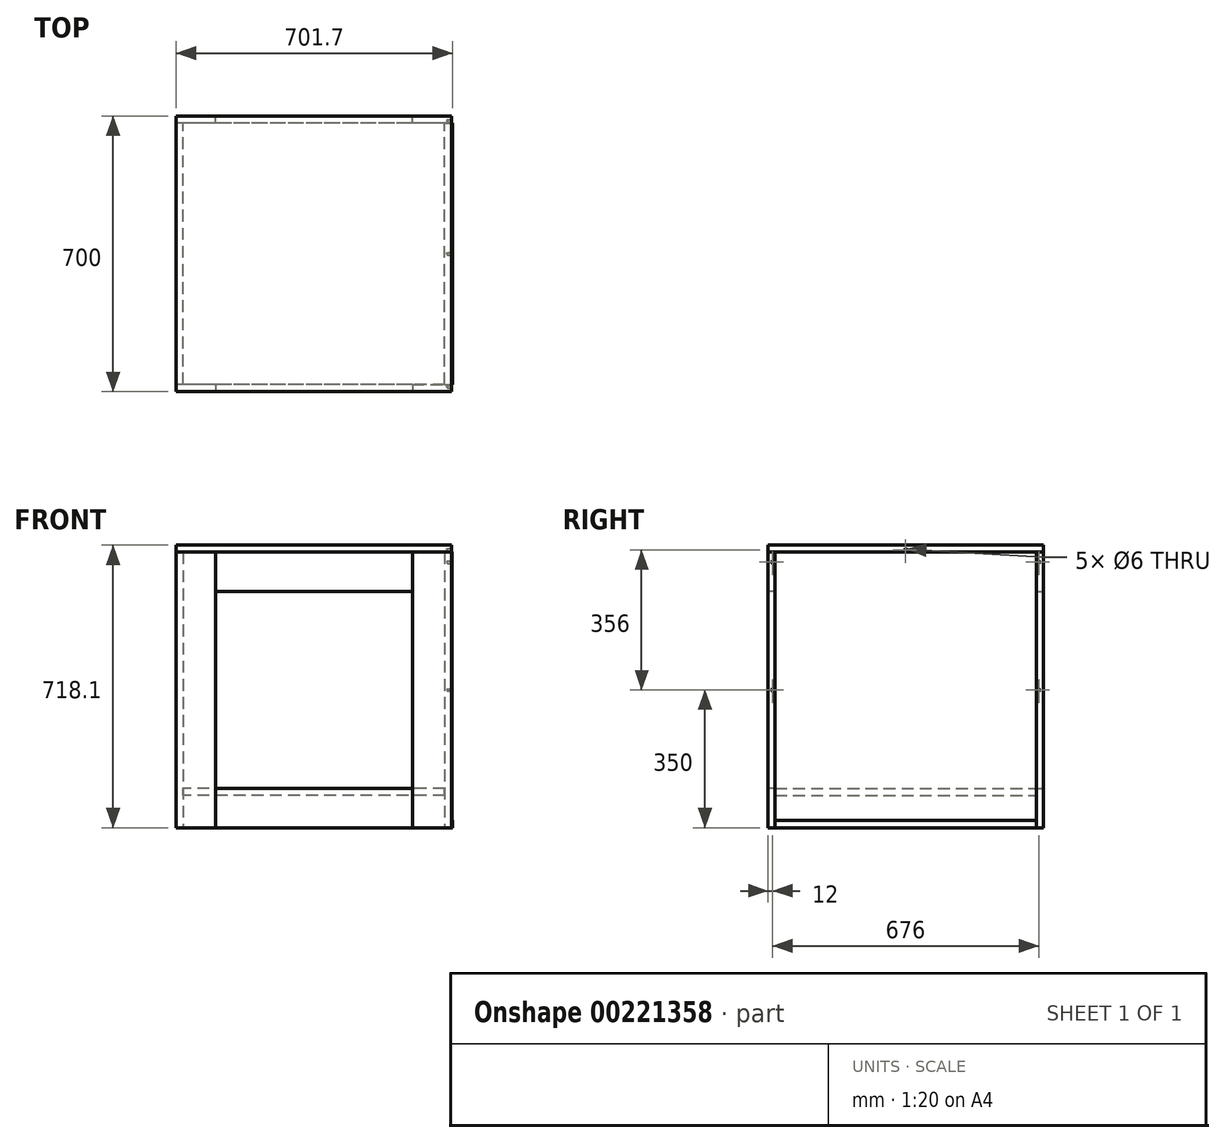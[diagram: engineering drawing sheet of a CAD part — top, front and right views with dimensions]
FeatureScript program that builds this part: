
annotation { "Feature Type Name" : "Feature", "Feature Type Description" : "" }
export const myFeature = defineFeature(function(context is Context, id is Id, definition is map)
    precondition{}
    {
        {
            var Q0;
            Q0=qCreatedBy(makeId("Top.planeOp"),FACE);
            var sketch = newSketch(context, id + "F0", { "sketchPlane" : qUnion([Q0])});
            skLineSegment(sketch, "E0.bottom", {"start": v(350, -350) * mm, "end": v(-350, -350) * mm});
            skLineSegment(sketch, "E0.top", {"start": v(350, 350) * mm, "end": v(-350, 350) * mm});
            skLineSegment(sketch, "E0.left", {"start": v(350, -350) * mm, "end": v(350, 350) * mm});
            skLineSegment(sketch, "E0.right", {"start": v(-350, -350) * mm, "end": v(-350, 350) * mm});
            skPoint(sketch, "E0.middle", {"position": v(0, 0) * mm});
            skLineSegment(sketch, "E1.0", {"start": v(332, 332) * mm, "end": v(-332, 332) * mm});
            skLineSegment(sketch, "E1.1", {"start": v(332, -332) * mm, "end": v(332, 332) * mm});
            skLineSegment(sketch, "E1.2", {"start": v(332, -332) * mm, "end": v(-332, -332) * mm});
            skLineSegment(sketch, "E1.3", {"start": v(-332, -332) * mm, "end": v(-332, 332) * mm});
            skLineSegment(sketch, "E2", {"start": v(-332, 332) * mm, "end": v(-350, 332) * mm});
            skLineSegment(sketch, "E3", {"start": v(-332, -332) * mm, "end": v(-350, -332) * mm});
            skLineSegment(sketch, "E4", {"start": v(-250, -332) * mm, "end": v(-250, -350) * mm});
            skLineSegment(sketch, "E5.MirrorCS", {"start": v(-250, 332) * mm, "end": v(-250, 350) * mm});
            skLineSegment(sketch, "E6.MirrorCS", {"start": v(250, 332) * mm, "end": v(250, 350) * mm});
            skLineSegment(sketch, "E7.MirrorCS", {"start": v(332, 332) * mm, "end": v(350, 332) * mm});
            skLineSegment(sketch, "E8.MirrorCS", {"start": v(332, -332) * mm, "end": v(350, -332) * mm});
            skLineSegment(sketch, "E9.MirrorCS", {"start": v(250, -332) * mm, "end": v(250, -350) * mm});
            skSolve(sketch);
        }
        {
            var Q0;
            {var subQ0=sQuery(id+"F0.wireOp",EDGE,"E3");Q0=makeQuery(id+"F0.imprint","IMPRINT",FACE,{"disambiguationData":[TD([[makeQuery(id+"F0.imprint","IMPRINT",EDGE,{"derivedFrom":subQ0}),1.0]])]});}
            var Q1;
            {var subQ0=sQuery(id+"F0.wireOp",EDGE,"E8.MirrorCS");Q1=makeQuery(id+"F0.imprint","IMPRINT",FACE,{"disambiguationData":[TD([[makeQuery(id+"F0.imprint","IMPRINT",EDGE,{"derivedFrom":subQ0}),-1.0]])]});}
            var Q2;
            {var subQ4=sQuery(id+"F0.wireOp",EDGE,"E6.MirrorCS");Q2=makeQuery(id+"F0.imprint","IMPRINT",FACE,{"disambiguationData":[TD([[makeQuery(id+"F0.imprint","IMPRINT",EDGE,{"derivedFrom":subQ4}),-1.0]])]});}
            var Q3;
            {var subQ0=sQuery(id+"F0.wireOp",EDGE,"E2");Q3=makeQuery(id+"F0.imprint","IMPRINT",FACE,{"disambiguationData":[TD([[makeQuery(id+"F0.imprint","IMPRINT",EDGE,{"derivedFrom":subQ0}),-1.0]])]});}
            extrude(context, id + "F1", {"entities" : qUnion([Q0, Q1, Q2, Q3]), "depth" : 700 * mm, "offsetDistance" : 25 * mm});
        }
        {
            var Q0;
            Q0=makeQuery(id+"F0.imprint","IMPRINT",FACE,{"disambiguationData":[TD([[makeQuery(id+"F0.imprint","IMPRINT",EDGE,{"derivedFrom":sQuery(id+"F0.wireOp",EDGE,"E1.3")}),1.0]])]});
            var Q1;
            Q1=makeQuery(id+"F0.imprint","IMPRINT",FACE,{"disambiguationData":[TD([[makeQuery(id+"F0.imprint","IMPRINT",EDGE,{"derivedFrom":sQuery(id+"F0.wireOp",EDGE,"E1.1")}),-1.0]])]});
            var Q2;
            Q2=makeQuery(id+"F1.opExtrude","CAP_FACE",FACE,{"disambiguationData":[OSD([sQuery(id+"F0.wireOp",EDGE,"E0.top"),sQuery(id+"F0.wireOp",EDGE,"E0.right"),sQuery(id+"F0.wireOp",EDGE,"E1.0"),sQuery(id+"F0.wireOp",EDGE,"E2"),sQuery(id+"F0.wireOp",EDGE,"E5.MirrorCS")])],"isStart":false});
            extrude(context, id + "F2", {"entities" : qUnion([Q0, Q1]), "endBound" : BoundingType.UP_TO_SURFACE, "depth" : 25 * mm, "endBoundEntityFace" : qUnion([Q2]), "offsetDistance" : 25 * mm});
        }
        {
            var Q0;
            {var subQ2=sQuery(id+"F0.wireOp",EDGE,"E4");Q0=makeQuery(id+"F0.imprint","IMPRINT",FACE,{"disambiguationData":[TD([[makeQuery(id+"F0.imprint","IMPRINT",EDGE,{"derivedFrom":subQ2}),1.0]])]});}
            var Q1;
            {var subQ2=sQuery(id+"F0.wireOp",EDGE,"E5.MirrorCS");Q1=makeQuery(id+"F0.imprint","IMPRINT",FACE,{"disambiguationData":[TD([[makeQuery(id+"F0.imprint","IMPRINT",EDGE,{"derivedFrom":subQ2}),-1.0]])]});}
            extrude(context, id + "F3", {"entities" : qUnion([Q0, Q1]), "depth" : 100 * mm, "offsetDistance" : 25 * mm});
        }
        {
            var Q0;
            Q0=makeQuery(id+"F1.opExtrude","CAP_FACE",FACE,{"disambiguationData":[OSD([sQuery(id+"F0.wireOp",EDGE,"E0.bottom"),sQuery(id+"F0.wireOp",EDGE,"E0.right"),sQuery(id+"F0.wireOp",EDGE,"E1.2"),sQuery(id+"F0.wireOp",EDGE,"E3"),sQuery(id+"F0.wireOp",EDGE,"E4")])],"isStart":false});
            var sketch = newSketch(context, id + "F4", { "sketchPlane" : qUnion([Q0])});
            skLineSegment(sketch, "E10.0", {"start": v(-250, -332) * mm, "end": v(-250, -350) * mm});
            skLineSegment(sketch, "E10.1", {"start": v(250, -332) * mm, "end": v(-250, -332) * mm});
            skLineSegment(sketch, "E10.2", {"start": v(250, -350) * mm, "end": v(-250, -350) * mm});
            skLineSegment(sketch, "E10.3", {"start": v(250, -332) * mm, "end": v(250, -350) * mm});
            skLineSegment(sketch, "E10.4", {"start": v(250, 332) * mm, "end": v(-250, 332) * mm});
            skLineSegment(sketch, "E10.5", {"start": v(250, 350) * mm, "end": v(-250, 350) * mm});
            skLineSegment(sketch, "E10.6", {"start": v(-250, 332) * mm, "end": v(-250, 350) * mm});
            skLineSegment(sketch, "E10.7", {"start": v(250, 332) * mm, "end": v(250, 350) * mm});
            skSolve(sketch);
        }
        {
            var Q0;
            Q0=makeQuery(id+"F4.imprint","IMPRINT",FACE,{"disambiguationData":[TD([[makeQuery(id+"F4.imprint","IMPRINT",EDGE,{"derivedFrom":sQuery(id+"F4.wireOp",EDGE,"E10.4")}),-1.0]])]});
            var Q1;
            Q1=makeQuery(id+"F4.imprint","IMPRINT",FACE,{"disambiguationData":[TD([[makeQuery(id+"F4.imprint","IMPRINT",EDGE,{"derivedFrom":sQuery(id+"F4.wireOp",EDGE,"E10.0")}),1.0]])]});
            extrude(context, id + "F5", {"entities" : qUnion([Q0, Q1]), "oppositeDirection" : true, "depth" : 100 * mm, "offsetDistance" : 25 * mm});
        }
        {
            var Q0;
            Q0=makeQuery(id+"F3.opExtrude","CAP_FACE",FACE,{"disambiguationData":[OSD([sQuery(id+"F0.wireOp",EDGE,"E0.top"),sQuery(id+"F0.wireOp",EDGE,"E1.0"),sQuery(id+"F0.wireOp",EDGE,"E5.MirrorCS"),sQuery(id+"F0.wireOp",EDGE,"E6.MirrorCS")])],"isStart":false});
            var sketch = newSketch(context, id + "F6", { "sketchPlane" : qUnion([Q0])});
            skLineSegment(sketch, "E11.0", {"start": v(332, 332) * mm, "end": v(-332, 332) * mm});
            skLineSegment(sketch, "E11.1", {"start": v(-332, -332) * mm, "end": v(-332, 332) * mm});
            skLineSegment(sketch, "E11.2", {"start": v(332, -332) * mm, "end": v(-332, -332) * mm});
            skLineSegment(sketch, "E11.3", {"start": v(332, -332) * mm, "end": v(332, 332) * mm});
            skSolve(sketch);
        }
        {
            var Q0;
            {var subQ0=sQuery(id+"F6.wireOp",EDGE,"E11.1");Q0=makeQuery(id+"F6.imprint","IMPRINT",FACE,{"disambiguationData":[TD([[makeQuery(id+"F6.imprint","IMPRINT",EDGE,{"derivedFrom":subQ0}),-1.0]])]});}
            extrude(context, id + "F7", {"entities" : qUnion([Q0]), "oppositeDirection" : true, "depth" : 18 * mm, "offsetDistance" : 25 * mm});
        }
        {
            var Q0;
            Q0=makeQuery(id+"F2.opExtrude","CAP_FACE",FACE,{"disambiguationData":[OSD([sQuery(id+"F0.wireOp",EDGE,"E0.right"),sQuery(id+"F0.wireOp",EDGE,"E1.3"),sQuery(id+"F0.wireOp",EDGE,"E2"),sQuery(id+"F0.wireOp",EDGE,"E3")])],"isStart":false});
            var sketch = newSketch(context, id + "F8", { "sketchPlane" : qUnion([Q0])});
            skLineSegment(sketch, "E12.0", {"start": v(-250, 350) * mm, "end": v(-350, 350) * mm});
            skLineSegment(sketch, "E12.1", {"start": v(250, 350) * mm, "end": v(-250, 350) * mm});
            skLineSegment(sketch, "E12.2", {"start": v(-350, -332) * mm, "end": v(-350, 332) * mm});
            skLineSegment(sketch, "E12.3", {"start": v(-350, 332) * mm, "end": v(-350, 350) * mm});
            skLineSegment(sketch, "E12.4", {"start": v(-250, -350) * mm, "end": v(-350, -350) * mm});
            skLineSegment(sketch, "E12.5", {"start": v(-350, -350) * mm, "end": v(-350, -332) * mm});
            skLineSegment(sketch, "E12.6", {"start": v(250, -350) * mm, "end": v(-250, -350) * mm});
            skLineSegment(sketch, "E12.7", {"start": v(350, -350) * mm, "end": v(250, -350) * mm});
            skLineSegment(sketch, "E12.8", {"start": v(350, -350) * mm, "end": v(350, -332) * mm});
            skLineSegment(sketch, "E12.9", {"start": v(350, -332) * mm, "end": v(350, 332) * mm});
            skLineSegment(sketch, "E12.10", {"start": v(350, 332) * mm, "end": v(350, 350) * mm});
            skLineSegment(sketch, "E12.11", {"start": v(350, 350) * mm, "end": v(250, 350) * mm});
            skSolve(sketch);
        }
        {
            var Q0;
            Q0=makeQuery(id+"F8.imprint","IMPRINT",FACE,{"disambiguationData":[TD([[makeQuery(id+"F8.imprint","IMPRINT",EDGE,{"derivedFrom":sQuery(id+"F8.wireOp",EDGE,"E12.0")}),1.0]])]});
            var Q1;
            Q1=makeQuery(id+"F8.imprint","IMPRINT",FACE,{"disambiguationData":[TD([[makeQuery(id+"F8.imprint","IMPRINT",EDGE,{"derivedFrom":sQuery(id+"F8.wireOp",EDGE,"E12.2")}),-1.0]])]});
            extrude(context, id + "F9", {"entities" : qUnion([Q0, Q1]), "depth" : 18 * mm, "offsetDistance" : 25 * mm});
        }
        {
            var Q0;
            Q0=makeQuery(id+"F9.opExtrude","CAP_FACE",FACE,{"disambiguationData":[OSD([sQuery(id+"F8.wireOp",EDGE,"E12.0"),sQuery(id+"F8.wireOp",EDGE,"E12.1"),sQuery(id+"F8.wireOp",EDGE,"E12.2"),sQuery(id+"F8.wireOp",EDGE,"E12.3"),sQuery(id+"F8.wireOp",EDGE,"E12.4"),sQuery(id+"F8.wireOp",EDGE,"E12.5"),sQuery(id+"F8.wireOp",EDGE,"E12.6"),sQuery(id+"F8.wireOp",EDGE,"E12.7"),sQuery(id+"F8.wireOp",EDGE,"E12.8"),sQuery(id+"F8.wireOp",EDGE,"E12.9"),sQuery(id+"F8.wireOp",EDGE,"E12.10"),sQuery(id+"F8.wireOp",EDGE,"E12.11")])],"isStart":false});
            extrude(context, id + "F10", {"entities" : qUnion([Q0]), "depth" : 0.1 * mm, "offsetDistance" : 25 * mm});
        }
        {
            var Q0;
            Q0=makeQuery(id+"F2.opExtrude","SWEPT_FACE",FACE,{"disambiguationData":[OSD([sQuery(id+"F0.wireOp",EDGE,"E0.right")])]});
            extrude(context, id + "F11", {"entities" : qUnion([Q0]), "depth" : 0.1 * mm, "offsetDistance" : 25 * mm});
        }
        {
            var Q0;
            Q0=makeQuery(id+"F2.opExtrude","SWEPT_FACE",FACE,{"disambiguationData":[OSD([sQuery(id+"F0.wireOp",EDGE,"E0.left")])]});
            var sketch = newSketch(context, id + "F12", { "sketchPlane" : qUnion([Q0])});
            skLineSegment(sketch, "E13.0", {"start": v(-332, 700) * mm, "end": v(332, 700) * mm});
            skLineSegment(sketch, "E13.1", {"start": v(-332, 700) * mm, "end": v(-332, 0) * mm});
            skLineSegment(sketch, "E13.2", {"start": v(332, 700) * mm, "end": v(332, 0) * mm});
            skLineSegment(sketch, "E13.3", {"start": v(-332, 0) * mm, "end": v(332, 0) * mm});
            skLineSegment(sketch, "E14", {"start": v(-332, 18) * mm, "end": v(332, 18) * mm});
            skSolve(sketch);
        }
        {
            var Q0;
            {var subQ0=sQuery(id+"F12.wireOp",EDGE,"E13.0");Q0=makeQuery(id+"F12.imprint","IMPRINT",FACE,{"disambiguationData":[TD([[makeQuery(id+"F12.imprint","IMPRINT",EDGE,{"derivedFrom":subQ0}),-1.0]])]});}
            extrude(context, id + "F13", {"entities" : qUnion([Q0]), "depth" : 0.1 * mm, "offsetDistance" : 25 * mm});
        }
        {
            var Q0;
            Q0=makeQuery(id+"F13.opExtrude","CAP_FACE",FACE,{"disambiguationData":[OSD([sQuery(id+"F12.wireOp",EDGE,"E13.0"),sQuery(id+"F12.wireOp",EDGE,"E13.1"),sQuery(id+"F12.wireOp",EDGE,"E13.2"),sQuery(id+"F12.wireOp",EDGE,"E14")])],"isStart":false});
            var sketch = newSketch(context, id + "F14", { "sketchPlane" : qUnion([Q0])});
            skLineSegment(sketch, "E15.0", {"start": v(-332, 700) * mm, "end": v(-332, 0) * mm});
            skLineSegment(sketch, "E15.1", {"start": v(-332, 0) * mm, "end": v(332, 0) * mm});
            skLineSegment(sketch, "E15.2", {"start": v(332, 700) * mm, "end": v(332, 0) * mm});
            skLineSegment(sketch, "E15.3", {"start": v(-332, 700) * mm, "end": v(332, 700) * mm});
            skSolve(sketch);
        }
        {
            var Q0;
            {var subQ2=sQuery(id+"F14.wireOp",EDGE,"E15.1");Q0=makeQuery(id+"F14.imprint","IMPRINT",FACE,{"disambiguationData":[TD([[makeQuery(id+"F14.imprint","IMPRINT",EDGE,{"derivedFrom":subQ2}),1.0]])]});}
            var Q1;
            {var subQ0=sQuery(id+"F14.wireOp",EDGE,"E15.3");Q1=makeQuery(id+"F14.imprint","IMPRINT",FACE,{"disambiguationData":[TD([[makeQuery(id+"F14.imprint","IMPRINT",EDGE,{"derivedFrom":subQ0}),-1.0]])]});}
            extrude(context, id + "F15", {"entities" : qUnion([Q0, Q1]), "depth" : 1 * mm, "offsetDistance" : 25 * mm});
        }
        {
            var Q0;
            Q0=makeQuery(id+"F15.opExtrude","CAP_FACE",FACE,{"disambiguationData":[OSD([sQuery(id+"F14.wireOp",EDGE,"E15.0"),sQuery(id+"F14.wireOp",EDGE,"E15.1"),sQuery(id+"F14.wireOp",EDGE,"E15.2"),sQuery(id+"F14.wireOp",EDGE,"E15.3")])],"isStart":false});
            var sketch = newSketch(context, id + "F16", { "sketchPlane" : qUnion([Q0])});
            skLineSegment(sketch, "E16.0", {"start": v(-332, 18) * mm, "end": v(332, 18) * mm});
            skLineSegment(sketch, "E16.1", {"start": v(-332, 700) * mm, "end": v(-332, 0) * mm});
            skLineSegment(sketch, "E16.2", {"start": v(-332, 0) * mm, "end": v(332, 0) * mm});
            skLineSegment(sketch, "E16.3", {"start": v(332, 700) * mm, "end": v(332, 0) * mm});
            skSolve(sketch);
        }
        {
            var Q0;
            {var subQ0=sQuery(id+"F16.wireOp",EDGE,"E16.0");Q0=makeQuery(id+"F16.imprint","IMPRINT",FACE,{"disambiguationData":[TD([[makeQuery(id+"F16.imprint","IMPRINT",EDGE,{"derivedFrom":subQ0}),-1.0]])]});}
            extrude(context, id + "F17", {"entities" : qUnion([Q0]), "depth" : 0.5 * mm, "offsetDistance" : 25 * mm});
        }
        {
            var Q0;
            {var subQ0=sQuery(id+"F0.wireOp",EDGE,"E0.left");Q0=makeQuery(id+"F1.opExtrude","SWEPT_FACE",FACE,{"disambiguationData":[OSD([subQ0]),TDD([makeQuery(id+"F0.imprint","IMPRINT",EDGE,{"disambiguationData":[TD([[makeQuery(id+"F0.imprint","INTERSECT",VERTEX,{"derivedFrom":[subQ0,sQuery(id+"F0.wireOp",EDGE,"E8.MirrorCS")]}),1.0]])],"derivedFrom":subQ0})])]});}
            var sketch = newSketch(context, id + "F18", { "sketchPlane" : qUnion([Q0])});
            skLineSegment(sketch, "E17.0", {"start": v(-332, 700) * mm, "end": v(-332, 0) * mm});
            skLineSegment(sketch, "E18.0", {"start": v(-332, 700) * mm, "end": v(332, 700) * mm});
            skPoint(sketch, "E19", {"position": v(-338, 350) * mm});
            skPoint(sketch, "E19.positionSnap0", {"position": v(-332, 350) * mm});
            skPoint(sketch, "E20", {"position": v(-338, 675) * mm});
            skPoint(sketch, "E21", {"position": v(0, 706) * mm});
            skPoint(sketch, "E22.MirrorP", {"position": v(338, 350) * mm});
            skPoint(sketch, "E23.MirrorP", {"position": v(338, 675) * mm});
            skSolve(sketch);
        }
        {
            var Q0;
            Q0=sQuery(id+"F18.wireOp",VERTEX,"E20");
            var Q1;
            Q1=sQuery(id+"F18.wireOp",VERTEX,"E21");
            var Q2;
            Q2=sQuery(id+"F18.wireOp",VERTEX,"E23.MirrorP");
            var Q3;
            Q3=sQuery(id+"F18.wireOp",VERTEX,"E22.MirrorP");
            var Q4;
            Q4=sQuery(id+"F18.wireOp",VERTEX,"E19");
            var Q5;
            Q5=makeQuery(id+"F1.opExtrude","SWEPT_BODY",BODY,{"disambiguationData":[OSD([sQuery(id+"F0.wireOp",EDGE,"E0.bottom"),sQuery(id+"F0.wireOp",EDGE,"E0.right"),sQuery(id+"F0.wireOp",EDGE,"E1.2"),sQuery(id+"F0.wireOp",EDGE,"E3"),sQuery(id+"F0.wireOp",EDGE,"E4")])]});
            var Q6;
            Q6=makeQuery(id+"F1.opExtrude","SWEPT_BODY",BODY,{"disambiguationData":[OSD([sQuery(id+"F0.wireOp",EDGE,"E0.bottom"),sQuery(id+"F0.wireOp",EDGE,"E0.left"),sQuery(id+"F0.wireOp",EDGE,"E1.2"),sQuery(id+"F0.wireOp",EDGE,"E8.MirrorCS"),sQuery(id+"F0.wireOp",EDGE,"E9.MirrorCS")])]});
            var Q7;
            Q7=makeQuery(id+"F1.opExtrude","SWEPT_BODY",BODY,{"disambiguationData":[OSD([sQuery(id+"F0.wireOp",EDGE,"E0.top"),sQuery(id+"F0.wireOp",EDGE,"E0.left"),sQuery(id+"F0.wireOp",EDGE,"E1.0"),sQuery(id+"F0.wireOp",EDGE,"E6.MirrorCS"),sQuery(id+"F0.wireOp",EDGE,"E7.MirrorCS")])]});
            var Q8;
            Q8=makeQuery(id+"F1.opExtrude","SWEPT_BODY",BODY,{"disambiguationData":[OSD([sQuery(id+"F0.wireOp",EDGE,"E0.top"),sQuery(id+"F0.wireOp",EDGE,"E0.right"),sQuery(id+"F0.wireOp",EDGE,"E1.0"),sQuery(id+"F0.wireOp",EDGE,"E2"),sQuery(id+"F0.wireOp",EDGE,"E5.MirrorCS")])]});
            var Q9;
            Q9=makeQuery(id+"F5.opExtrude","SWEPT_BODY",BODY,{"disambiguationData":[OSD([sQuery(id+"F4.wireOp",EDGE,"E10.0"),sQuery(id+"F4.wireOp",EDGE,"E10.1"),sQuery(id+"F4.wireOp",EDGE,"E10.2"),sQuery(id+"F4.wireOp",EDGE,"E10.3")])]});
            var Q10;
            Q10=makeQuery(id+"F5.opExtrude","SWEPT_BODY",BODY,{"disambiguationData":[OSD([sQuery(id+"F4.wireOp",EDGE,"E10.4"),sQuery(id+"F4.wireOp",EDGE,"E10.5"),sQuery(id+"F4.wireOp",EDGE,"E10.6"),sQuery(id+"F4.wireOp",EDGE,"E10.7")])]});
            var Q11;
            Q11=makeQuery(id+"F9.opExtrude","SWEPT_BODY",BODY,{"disambiguationData":[OSD([sQuery(id+"F8.wireOp",EDGE,"E12.0"),sQuery(id+"F8.wireOp",EDGE,"E12.1"),sQuery(id+"F8.wireOp",EDGE,"E12.2"),sQuery(id+"F8.wireOp",EDGE,"E12.3"),sQuery(id+"F8.wireOp",EDGE,"E12.4"),sQuery(id+"F8.wireOp",EDGE,"E12.5"),sQuery(id+"F8.wireOp",EDGE,"E12.6"),sQuery(id+"F8.wireOp",EDGE,"E12.7"),sQuery(id+"F8.wireOp",EDGE,"E12.8"),sQuery(id+"F8.wireOp",EDGE,"E12.9"),sQuery(id+"F8.wireOp",EDGE,"E12.10"),sQuery(id+"F8.wireOp",EDGE,"E12.11")])]});
            hole(context, id + "F19", {"style" : HoleStyle.SIMPLE, "endStyle" : HoleEndStyle.BLIND, "holeDiameter" : 6 * mm, "majorDiameter" : 5 * mm, "holeDepth" : 11 * mm, "isTappedThrough" : true, "tappedDepth" : 4.9 * mm, "tapClearance" : 3, "startFromSketch" : true, "locations" : qUnion([Q0, Q1, Q2, Q3, Q4]), "scope" : qUnion([Q5, Q6, Q7, Q8, Q9, Q10, Q11])});
        }
    });
